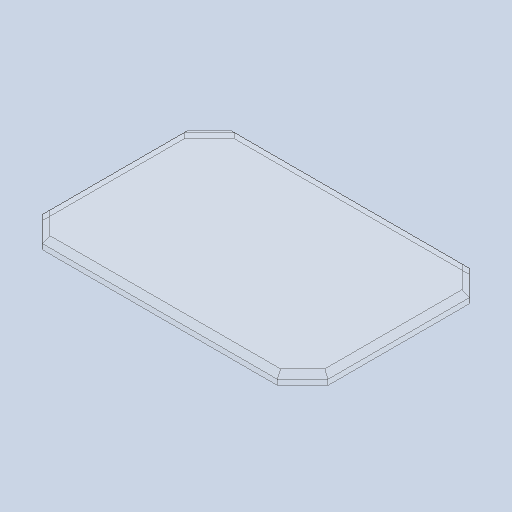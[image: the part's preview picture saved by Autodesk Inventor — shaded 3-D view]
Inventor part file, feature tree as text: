
AUTODESK INVENTOR PART (.ipt)
format: ipt  version: 2024 (Build 280153000, 153)  size: 259,072 bytes
history: native  units: in
note: dims shown in document units (in); Inventor stores cm internally (conversion verified against a paired STEP export)
features: extrude x1, chamfer x1, sketch x1
ambient origin geometry x8: Origin, YZ Plane, XZ Plane, XY Plane, X Axis, Y Axis, Z Axis, Center Point
bodies: Body1 (feature_tree)
feature tree (3):
  extrude  "Extrusion3"  Depth=1.0in TaperAngle=45.0deg
  chamfer  "Chamfer1"  [1 undecoded]
  sketch  "Sketch3"  dims[d6=1.0in d7=0.0in d8=0.5in d9=0.125in d10=45.0deg]
note: 1 required parameter value undecoded (feature->parameter linkage not recoverable at this tier; creation-order binding heuristic only, values carry confidence <= 0.55)
